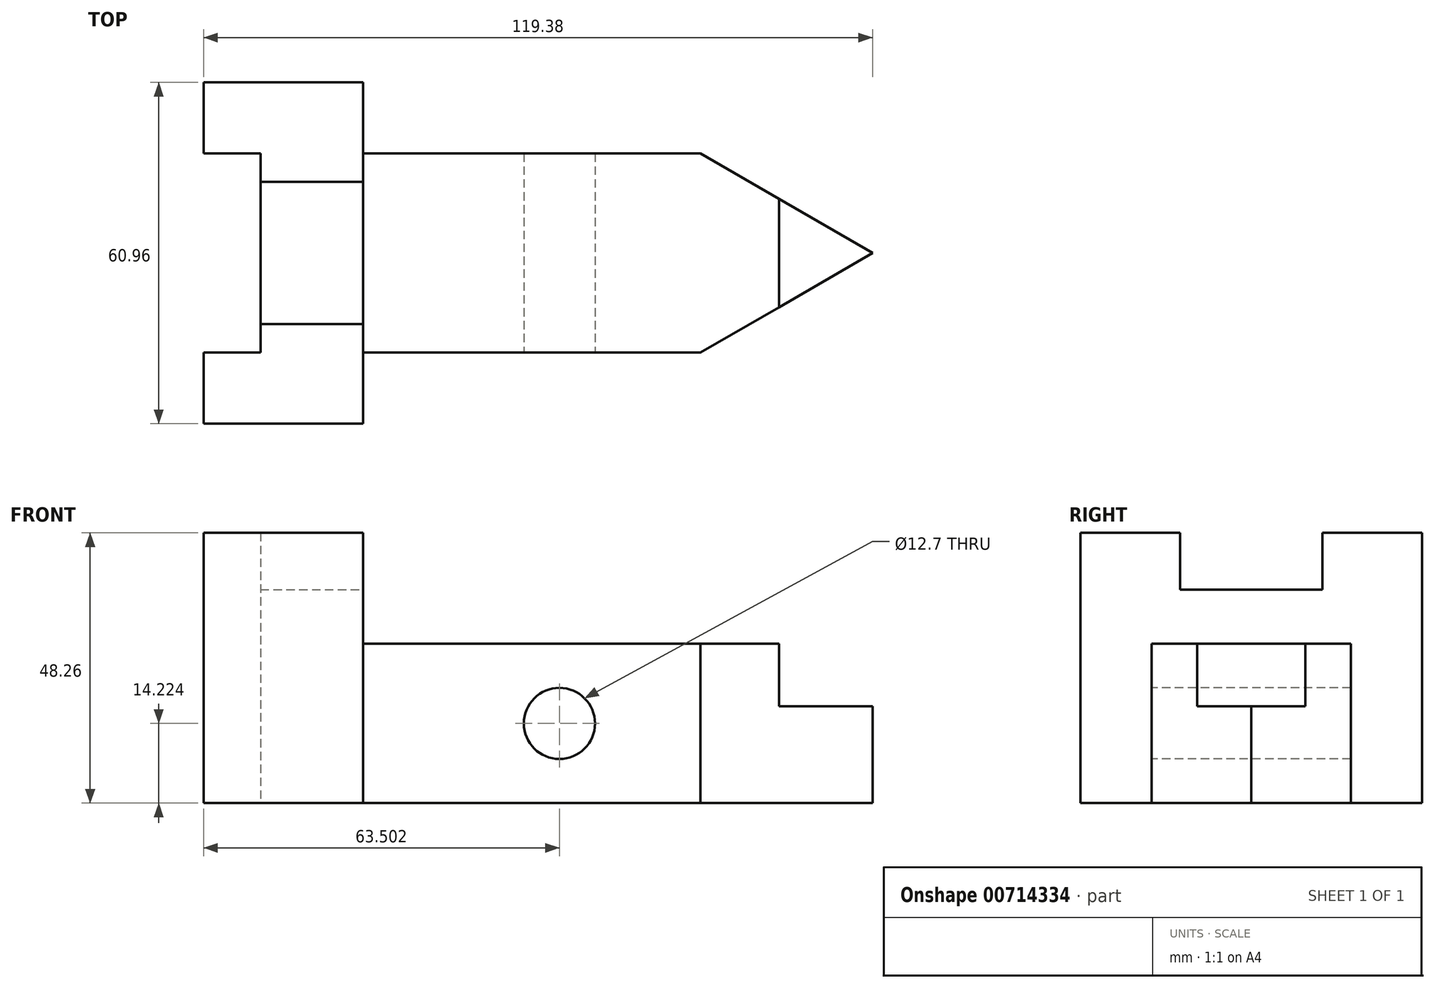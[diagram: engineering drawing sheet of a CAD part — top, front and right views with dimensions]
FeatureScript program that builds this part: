
annotation { "Feature Type Name" : "Feature", "Feature Type Description" : "" }
export const myFeature = defineFeature(function(context is Context, id is Id, definition is map)
    precondition{}
    {
        {
            var Q0;
            Q0=qCreatedBy(makeId("Top.planeOp"),FACE);
            var sketch = newSketch(context, id + "F0", { "sketchPlane" : qUnion([Q0])});
            skLineSegment(sketch, "E0", {"start": v(0, 0) * mm, "end": v(-28.45, 0) * mm});
            skLineSegment(sketch, "E1", {"start": v(-28.45, 0) * mm, "end": v(-28.45, 12.7) * mm});
            skLineSegment(sketch, "E2", {"start": v(-28.45, 12.7) * mm, "end": v(-18.29, 12.7) * mm});
            skLineSegment(sketch, "E3", {"start": v(-18.29, 12.7) * mm, "end": v(-18.29, 17.78) * mm});
            skLineSegment(sketch, "E4", {"start": v(0, 0) * mm, "end": v(0, 30.48) * mm});
            skLineSegment(sketch, "E5", {"start": v(-18.29, 30.48) * mm, "end": v(-18.29, 17.78) * mm});
            skLineSegment(sketch, "E6.MirrorCS", {"start": v(-18.29, 30.48) * mm, "end": v(-18.29, 43.18) * mm});
            skLineSegment(sketch, "E7.MirrorCS", {"start": v(-28.45, 60.96) * mm, "end": v(-28.45, 48.26) * mm});
            skLineSegment(sketch, "E8.MirrorCS", {"start": v(-28.45, 48.26) * mm, "end": v(-18.29, 48.26) * mm});
            skLineSegment(sketch, "E9.MirrorCS", {"start": v(-18.29, 48.26) * mm, "end": v(-18.29, 43.18) * mm});
            skLineSegment(sketch, "E10.MirrorCS", {"start": v(0, 60.96) * mm, "end": v(-28.45, 60.96) * mm});
            skLineSegment(sketch, "E11.MirrorCS", {"start": v(0, 60.96) * mm, "end": v(0, 30.48) * mm});
            skSolve(sketch);
        }
        {
            var Q0;
            Q0 = qSketchRegion(id + "F0", true);
            extrude(context, id + "F1", {"entities" : qUnion([Q0]), "depth" : 48.26 * mm, "offsetDistance" : 25.4 * mm});
        }
        {
            var Q0;
            Q0=makeQuery(id+"F1.opExtrude","SWEPT_FACE",FACE,{"disambiguationData":[OSD([sQuery(id+"F0.wireOp",EDGE,"E4"),sQuery(id+"F0.wireOp",EDGE,"E11.MirrorCS")])]});
            var sketch = newSketch(context, id + "F2", { "sketchPlane" : qUnion([Q0])});
            skLineSegment(sketch, "E12", {"start": v(30.48, 38.1) * mm, "end": v(17.78, 38.1) * mm});
            skLineSegment(sketch, "E13", {"start": v(17.78, 38.1) * mm, "end": v(17.78, 48.26) * mm});
            skLineSegment(sketch, "E14", {"start": v(30.48, 48.26) * mm, "end": v(43.18, 48.26) * mm});
            skLineSegment(sketch, "E15", {"start": v(43.18, 48.26) * mm, "end": v(43.18, 38.1) * mm});
            skLineSegment(sketch, "E16", {"start": v(30.48, 38.1) * mm, "end": v(43.18, 38.1) * mm});
            skLineSegment(sketch, "E17", {"start": v(17.78, 48.26) * mm, "end": v(43.18, 48.26) * mm});
            skSolve(sketch);
        }
        {
            var Q0;
            Q0=makeQuery(id+"F2.imprint","IMPRINT",FACE,{"disambiguationData":[TD([[makeQuery(id+"F2.imprint","IMPRINT",EDGE,{"derivedFrom":sQuery(id+"F2.wireOp",EDGE,"E12")}),-1.0]])]});
            extrude(context, id + "F3", {"entities" : qUnion([Q0]), "operationType" : NewBodyOperationType.REMOVE, "endBound" : BoundingType.UP_TO_NEXT, "oppositeDirection" : true, "depth" : 25.4 * mm, "offsetDistance" : 25.4 * mm});
        }
        {
            var Q0;
            Q0=qCreatedBy(makeId("Top.planeOp"),FACE);
            var sketch = newSketch(context, id + "F4", { "sketchPlane" : qUnion([Q0])});
            skLineSegment(sketch, "E18", {"start": v(0, 0) * mm, "end": v(0, 30.48) * mm});
            skLineSegment(sketch, "E19", {"start": v(0, 30.48) * mm, "end": v(0, 48.26) * mm});
            skLineSegment(sketch, "E20", {"start": v(0, 48.26) * mm, "end": v(60.2, 48.26) * mm});
            skLineSegment(sketch, "E21", {"start": v(60.2, 48.26) * mm, "end": v(90.93, 30.48) * mm});
            skLineSegment(sketch, "E22.MirrorCS", {"start": v(0, 12.7) * mm, "end": v(60.2, 12.7) * mm});
            skLineSegment(sketch, "E23.MirrorCS", {"start": v(60.2, 12.7) * mm, "end": v(90.93, 30.48) * mm});
            skSolve(sketch);
        }
        {
            var Q0;
            {var subQ0=sQuery(id+"F4.wireOp",EDGE,"E19");Q0=makeQuery(id+"F4.imprint","IMPRINT",FACE,{"disambiguationData":[TD([[makeQuery(id+"F4.imprint","IMPRINT",EDGE,{"derivedFrom":subQ0}),-1.0]])]});}
            extrude(context, id + "F5", {"entities" : qUnion([Q0]), "operationType" : NewBodyOperationType.ADD, "depth" : 28.45 * mm, "offsetDistance" : 25.4 * mm});
        }
        {
            var Q0;
            Q0=makeQuery(id+"F5.opExtrude","CAP_FACE",FACE,{"disambiguationData":[OSD([sQuery(id+"F4.wireOp",EDGE,"E18"),sQuery(id+"F4.wireOp",EDGE,"E19"),sQuery(id+"F4.wireOp",EDGE,"E20"),sQuery(id+"F4.wireOp",EDGE,"E21"),sQuery(id+"F4.wireOp",EDGE,"E22.MirrorCS"),sQuery(id+"F4.wireOp",EDGE,"E23.MirrorCS")])],"isStart":false});
            var sketch = newSketch(context, id + "F6", { "sketchPlane" : qUnion([Q0])});
            skLineSegment(sketch, "E24", {"start": v(90.93, 30.48) * mm, "end": v(74.22, 40.15) * mm});
            skLineSegment(sketch, "E25", {"start": v(74.22, 40.15) * mm, "end": v(74.22, 20.81) * mm});
            skLineSegment(sketch, "E26", {"start": v(74.22, 20.81) * mm, "end": v(90.93, 30.48) * mm});
            skSolve(sketch);
        }
        {
            var Q0;
            Q0=makeQuery(id+"F6.imprint","IMPRINT",FACE,{"disambiguationData":[TD([[makeQuery(id+"F6.imprint","IMPRINT",EDGE,{"derivedFrom":sQuery(id+"F6.wireOp",EDGE,"E24")}),-1.0]])]});
            extrude(context, id + "F7", {"entities" : qUnion([Q0]), "operationType" : NewBodyOperationType.REMOVE, "oppositeDirection" : true, "depth" : 11.18 * mm, "offsetDistance" : 25.4 * mm});
        }
        {
            var Q0;
            Q0=makeQuery(id+"F5.opExtrude","SWEPT_FACE",FACE,{"disambiguationData":[OSD([sQuery(id+"F4.wireOp",EDGE,"E22.MirrorCS")])]});
            var sketch = newSketch(context, id + "F8", { "sketchPlane" : qUnion([Q0])});
            skCircle(sketch, "E27", {"center": v(35.05, 14.22) * mm, "radius": 6.35 * mm});
            skSolve(sketch);
        }
        {
            var Q0;
            Q0=makeQuery(id+"F8.imprint","IMPRINT",FACE,{"disambiguationData":[TD([[makeQuery(id+"F8.imprint","IMPRINT",EDGE,{"derivedFrom":sQuery(id+"F8.wireOp",EDGE,"E27")}),1.0]])]});
            extrude(context, id + "F9", {"entities" : qUnion([Q0]), "operationType" : NewBodyOperationType.REMOVE, "endBound" : BoundingType.UP_TO_NEXT, "oppositeDirection" : true, "depth" : 25.4 * mm, "offsetDistance" : 25.4 * mm});
        }
    });
